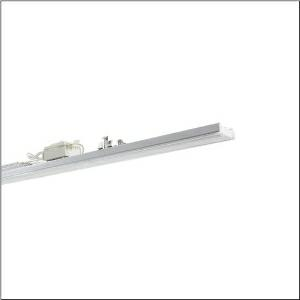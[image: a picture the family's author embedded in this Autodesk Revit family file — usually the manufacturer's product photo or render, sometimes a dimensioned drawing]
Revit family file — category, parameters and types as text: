
# Revit family: licross_r__11_recessed_mo_51tl18dv4e5g_1059
name_source: partatom
category: Lighting Fixtures
units: mm (PartAtom-declared; Revit-internal decimal feet)

## family parameters
Cut with Voids When Loaded = No
Host = Face
Light Source = No
Part Type = Normal
Room Calculation Point = No
Round Connector Dimension = Use Diameter
Shared = No

## types (1)
- --- (1 x LED, 14920 lm, 84.1 W, 4000K)
    Apparent Load = 84 VA
    CIE Flux Codes = 83 96 99 100 100
    Color Rendering = 80
    Color Temperature = 4000K
    Default Elevation = 1800 mm
    Description = Licross® 11 Recessed MO, luminaire insert, of sheet steel, coil coated, white, length: 2.250mm, width: 66mm, height: 67mm, LED rated luminous flux: 14.920lm, light colour: 840, control gear: DALI 2, with plug, 5-pole, with phase selection, mains connection: 220..240V, AC, 50/60Hz, rated input power: 84W, halogen-free wiring, primary light control with lens, of plastic, primary optical cover: cover, of PMMA, light emission: direct distribution, primary light characteristic: symmetric, protection rating (complete): IP40, insulation class (complete): insulation class I (protective earthing), certification: CE, ENEC, VDE, UKCA, protection symbol: D if used in an environment without relevant dust loads with corresponding accessories, impact resistance: IK06, permissible ambient temperature for indoor applications: -25..+35°C, corresponds to IFS (International Featured Standards) requirements for safety and quality in the food industry, reducing of maximum allowable ambient temperature of 5°C with ceiling mounting, LABS conformity tested according to VDMA 24364:2018-05, packaging unit: 1 piece
    Height = 58 mm
    Lamp = 1 x LED
    Lamp Light Flux = 14920 lm
    Lamp Power = 84.1 W
    Lamp count = 1
    Length = 2250 mm
    Luminous efficacy = 177 lm/W
    Manufacturer = Siteco
    ModVariant = No
    Model = 51TL18DV4E5G
    Mounting Place = Ceiling
    Mounting Type = Pendant
    Number of Poles = 1
    OnlyDefault = Yes
    Power Factor = 1
    Product Name = Licross® 11 Recessed MO
    Product group = luminaire insert
    ProductGroupID = 902
    Protection Class = Protection class I
    Protection Degree = IP 40
    RLX_Detail_Level = 1
    RLX_Emergency_Light_Flux = 0 lm
    RLX_Emergency_Type = 0
    RLX_Emergency_Type_DB = No
    RlxData = <blob elided: 29101 chars, md5=aab43d61>
    Socket = socket
    Standby Power = 0 W
    System Light Flux = 14920 lm
    System Power = 84 W
    Type Comments = factory setting: luminous flux: 100 % | dim-lin: 254 | 378 mA
    Type Image = l_1296930.jpg
    URL = http://relux.com
    VarID = @adj_099114
    Voltage = 0 V
    Weight = 0.00 kg
    Width = 66 mm

## geometry (parser evidence)
native form markers: Blend x4, Sweep x8
no freeform markers — native parametric forms only
